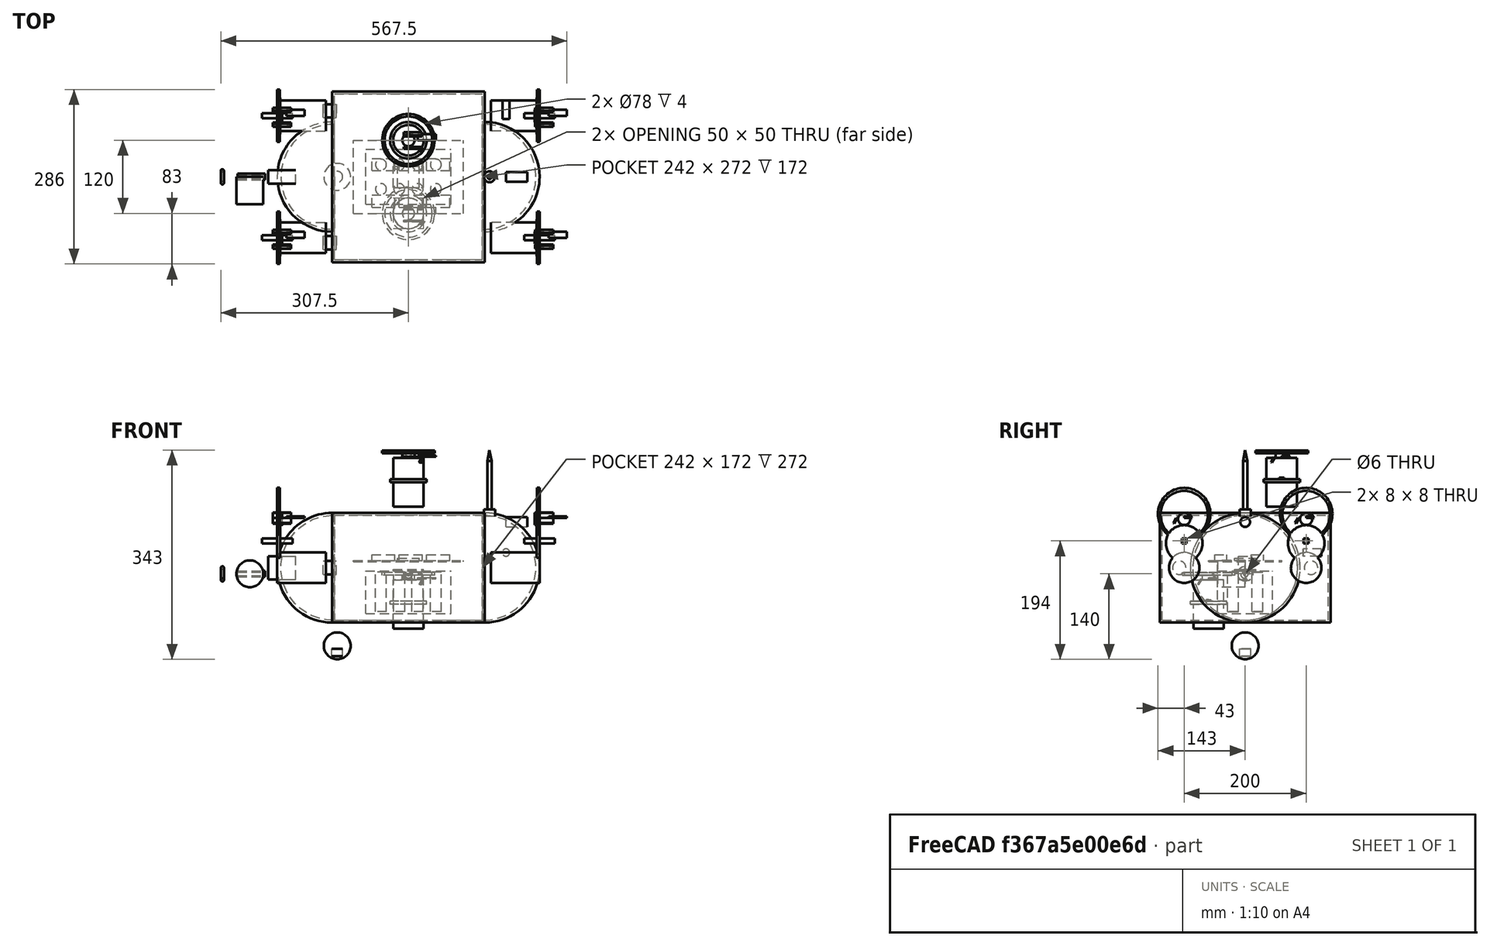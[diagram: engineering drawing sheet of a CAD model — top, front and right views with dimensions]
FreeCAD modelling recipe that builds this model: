
FCSTD DOCUMENT  (FreeCAD 0.19R)
Label: fishing_drone_detailed
License: All rights reserved
LicenseURL: http://en.wikipedia.org/wiki/All_rights_reserved
objects: Part::Cylinder×48, Part::Box×37, Part::MultiFuse×9, Part::Cut×8, Part::Sphere×5, Part::Torus×1, Part::Cone×1
note: 109 computed .brp shape members not serialized (recipe doc carries the construction recipe); baked Part::Feature solids carry a one-line shape summary decoded from their .brp

FEATURE [Part::Box] CenterBody
  AttacherType = Attacher::AttachEngine3D
  Height = 180
  Length = 250
  Placement = pos=(-125,-140,-90) rot=(0,0,1;0rad)
  Width = 280
FEATURE [Part::Sphere] Nose
  Angle1 = -90
  Angle2 = 90
  Angle3 = 360
  AttacherType = Attacher::AttachEngine3D
  Placement = pos=(-125,0,0) rot=(0,0,1;0rad)
  Radius = 90
FEATURE [Part::Sphere] Tail
  Angle1 = -90
  Angle2 = 90
  Angle3 = 360
  AttacherType = Attacher::AttachEngine3D
  Placement = pos=(125,0,0) rot=(0,0,1;0rad)
  Radius = 90
FEATURE [Part::MultiFuse] BodyOuter
  Shapes = -> [CenterBody,Nose,Tail]
FEATURE [Part::Box] CenterInner
  AttacherType = Attacher::AttachEngine3D
  Height = 172
  Length = 242
  Placement = pos=(-121,-136,-86) rot=(0,0,1;0rad)
  Width = 272
FEATURE [Part::Sphere] NoseInner
  Angle1 = -90
  Angle2 = 90
  Angle3 = 360
  AttacherType = Attacher::AttachEngine3D
  Placement = pos=(-123,0,0) rot=(0,0,1;0rad)
  Radius = 86
FEATURE [Part::Sphere] TailInner
  Angle1 = -90
  Angle2 = 90
  Angle3 = 360
  AttacherType = Attacher::AttachEngine3D
  Placement = pos=(123,0,0) rot=(0,0,1;0rad)
  Radius = 86
FEATURE [Part::MultiFuse] BodyInner
  Shapes = -> [CenterInner,NoseInner,TailInner]
FEATURE [Part::Cut] HollowBody
  Base = -> BodyOuter
  Tool = -> BodyInner
FEATURE [Part::Cylinder] Motor_FL
  Angle = 360
  AttacherType = Attacher::AttachEngine3D
  Height = 80
  Placement = pos=(-215,100,0) rot=(0,1,0;1.5708rad)
  Radius = 25
FEATURE [Part::Cylinder] Flange_FL
  Angle = 360
  AttacherType = Attacher::AttachEngine3D
  Height = 5
  Placement = pos=(-215,100,40) rot=(0,1,0;1.5708rad)
  Radius = 30
FEATURE [Part::Box] Blade_FL_0
  AttacherType = Attacher::AttachEngine3D
  Height = 2
  Length = 30
  Placement = pos=(-200,100,82) rot=(0,0,1;0rad)
  Width = 10
FEATURE [Part::Box] Blade_FL_1
  AttacherType = Attacher::AttachEngine3D
  Height = 2
  Length = 30
  Placement = pos=(-222.5,112.99,82) rot=(1,0,0;2.0944rad)
  Width = 10
FEATURE [Part::Box] Blade_FL_2
  AttacherType = Attacher::AttachEngine3D
  Height = 2
  Length = 30
  Placement = pos=(-222.5,87.0096,82) rot=(1,0,0;4.18879rad)
  Width = 10
FEATURE [Part::Cylinder] Hub_FL
  Angle = 360
  AttacherType = Attacher::AttachEngine3D
  Height = 8
  Placement = pos=(-215,100,80) rot=(0,1,0;1.5708rad)
  Radius = 10
FEATURE [Part::Cylinder] GuardOut_FL
  Angle = 360
  AttacherType = Attacher::AttachEngine3D
  Height = 4
  Placement = pos=(-215,100,88) rot=(0,1,0;1.5708rad)
  Radius = 43
FEATURE [Part::Cylinder] GuardIn_FL
  Angle = 360
  AttacherType = Attacher::AttachEngine3D
  Height = 6
  Placement = pos=(-215,100,87) rot=(0,1,0;1.5708rad)
  Radius = 39
FEATURE [Part::Cut] Guard_FL
  Base = -> GuardOut_FL
  Tool = -> GuardIn_FL
FEATURE [Part::Box] Arm_FL
  AttacherType = Attacher::AttachEngine3D
  Height = 8
  Length = 50
  Placement = pos=(-240,96,40) rot=(0,0,1;0rad)
  Width = 8
FEATURE [Part::MultiFuse] Thruster_FL
  Shapes = -> [Motor_FL,Flange_FL,Hub_FL,Guard_FL,Arm_FL,Blade_FL_0,Blade_FL_1,Blade_FL_2]
FEATURE [Part::Cylinder] Motor_FR
  Angle = 360
  AttacherType = Attacher::AttachEngine3D
  Height = 80
  Placement = pos=(-215,-100,0) rot=(0,1,0;1.5708rad)
  Radius = 25
FEATURE [Part::Cylinder] Flange_FR
  Angle = 360
  AttacherType = Attacher::AttachEngine3D
  Height = 5
  Placement = pos=(-215,-100,40) rot=(0,1,0;1.5708rad)
  Radius = 30
FEATURE [Part::Box] Blade_FR_0
  AttacherType = Attacher::AttachEngine3D
  Height = 2
  Length = 30
  Placement = pos=(-200,-100,82) rot=(0,0,1;0rad)
  Width = 10
FEATURE [Part::Box] Blade_FR_1
  AttacherType = Attacher::AttachEngine3D
  Height = 2
  Length = 30
  Placement = pos=(-222.5,-87.0096,82) rot=(1,0,0;2.0944rad)
  Width = 10
FEATURE [Part::Box] Blade_FR_2
  AttacherType = Attacher::AttachEngine3D
  Height = 2
  Length = 30
  Placement = pos=(-222.5,-112.99,82) rot=(1,0,0;4.18879rad)
  Width = 10
FEATURE [Part::Cylinder] Hub_FR
  Angle = 360
  AttacherType = Attacher::AttachEngine3D
  Height = 8
  Placement = pos=(-215,-100,80) rot=(0,1,0;1.5708rad)
  Radius = 10
FEATURE [Part::Cylinder] GuardOut_FR
  Angle = 360
  AttacherType = Attacher::AttachEngine3D
  Height = 4
  Placement = pos=(-215,-100,88) rot=(0,1,0;1.5708rad)
  Radius = 43
FEATURE [Part::Cylinder] GuardIn_FR
  Angle = 360
  AttacherType = Attacher::AttachEngine3D
  Height = 6
  Placement = pos=(-215,-100,87) rot=(0,1,0;1.5708rad)
  Radius = 39
FEATURE [Part::Cut] Guard_FR
  Base = -> GuardOut_FR
  Tool = -> GuardIn_FR
FEATURE [Part::Box] Arm_FR
  AttacherType = Attacher::AttachEngine3D
  Height = 8
  Length = 50
  Placement = pos=(-240,-104,40) rot=(0,0,1;0rad)
  Width = 8
FEATURE [Part::MultiFuse] Thruster_FR
  Shapes = -> [Motor_FR,Flange_FR,Hub_FR,Guard_FR,Arm_FR,Blade_FR_0,Blade_FR_1,Blade_FR_2]
FEATURE [Part::Cylinder] Motor_RL
  Angle = 360
  AttacherType = Attacher::AttachEngine3D
  Height = 80
  Placement = pos=(215,100,0) rot=(0,1,0;-1.5708rad)
  Radius = 25
FEATURE [Part::Cylinder] Flange_RL
  Angle = 360
  AttacherType = Attacher::AttachEngine3D
  Height = 5
  Placement = pos=(215,100,40) rot=(0,1,0;-1.5708rad)
  Radius = 30
FEATURE [Part::Box] Blade_RL_0
  AttacherType = Attacher::AttachEngine3D
  Height = 2
  Length = 30
  Placement = pos=(230,100,82) rot=(0,0,1;0rad)
  Width = 10
FEATURE [Part::Box] Blade_RL_1
  AttacherType = Attacher::AttachEngine3D
  Height = 2
  Length = 30
  Placement = pos=(207.5,112.99,82) rot=(1,0,0;2.0944rad)
  Width = 10
FEATURE [Part::Box] Blade_RL_2
  AttacherType = Attacher::AttachEngine3D
  Height = 2
  Length = 30
  Placement = pos=(207.5,87.0096,82) rot=(1,0,0;4.18879rad)
  Width = 10
FEATURE [Part::Cylinder] Hub_RL
  Angle = 360
  AttacherType = Attacher::AttachEngine3D
  Height = 8
  Placement = pos=(215,100,80) rot=(0,1,0;-1.5708rad)
  Radius = 10
FEATURE [Part::Cylinder] GuardOut_RL
  Angle = 360
  AttacherType = Attacher::AttachEngine3D
  Height = 4
  Placement = pos=(215,100,88) rot=(0,1,0;-1.5708rad)
  Radius = 43
FEATURE [Part::Cylinder] GuardIn_RL
  Angle = 360
  AttacherType = Attacher::AttachEngine3D
  Height = 6
  Placement = pos=(215,100,87) rot=(0,1,0;-1.5708rad)
  Radius = 39
FEATURE [Part::Cut] Guard_RL
  Base = -> GuardOut_RL
  Tool = -> GuardIn_RL
FEATURE [Part::Box] Arm_RL
  AttacherType = Attacher::AttachEngine3D
  Height = 8
  Length = 50
  Placement = pos=(190,96,40) rot=(0,0,1;0rad)
  Width = 8
FEATURE [Part::MultiFuse] Thruster_RL
  Shapes = -> [Motor_RL,Flange_RL,Hub_RL,Guard_RL,Arm_RL,Blade_RL_0,Blade_RL_1,Blade_RL_2]
FEATURE [Part::Cylinder] Motor_RR
  Angle = 360
  AttacherType = Attacher::AttachEngine3D
  Height = 80
  Placement = pos=(215,-100,0) rot=(0,1,0;-1.5708rad)
  Radius = 25
FEATURE [Part::Cylinder] Flange_RR
  Angle = 360
  AttacherType = Attacher::AttachEngine3D
  Height = 5
  Placement = pos=(215,-100,40) rot=(0,1,0;-1.5708rad)
  Radius = 30
FEATURE [Part::Box] Blade_RR_0
  AttacherType = Attacher::AttachEngine3D
  Height = 2
  Length = 30
  Placement = pos=(230,-100,82) rot=(0,0,1;0rad)
  Width = 10
FEATURE [Part::Box] Blade_RR_1
  AttacherType = Attacher::AttachEngine3D
  Height = 2
  Length = 30
  Placement = pos=(207.5,-87.0096,82) rot=(1,0,0;2.0944rad)
  Width = 10
FEATURE [Part::Box] Blade_RR_2
  AttacherType = Attacher::AttachEngine3D
  Height = 2
  Length = 30
  Placement = pos=(207.5,-112.99,82) rot=(1,0,0;4.18879rad)
  Width = 10
FEATURE [Part::Cylinder] Hub_RR
  Angle = 360
  AttacherType = Attacher::AttachEngine3D
  Height = 8
  Placement = pos=(215,-100,80) rot=(0,1,0;-1.5708rad)
  Radius = 10
FEATURE [Part::Cylinder] GuardOut_RR
  Angle = 360
  AttacherType = Attacher::AttachEngine3D
  Height = 4
  Placement = pos=(215,-100,88) rot=(0,1,0;-1.5708rad)
  Radius = 43
FEATURE [Part::Cylinder] GuardIn_RR
  Angle = 360
  AttacherType = Attacher::AttachEngine3D
  Height = 6
  Placement = pos=(215,-100,87) rot=(0,1,0;-1.5708rad)
  Radius = 39
FEATURE [Part::Cut] Guard_RR
  Base = -> GuardOut_RR
  Tool = -> GuardIn_RR
FEATURE [Part::Box] Arm_RR
  AttacherType = Attacher::AttachEngine3D
  Height = 8
  Length = 50
  Placement = pos=(190,-104,40) rot=(0,0,1;0rad)
  Width = 8
FEATURE [Part::MultiFuse] Thruster_RR
  Shapes = -> [Motor_RR,Flange_RR,Hub_RR,Guard_RR,Arm_RR,Blade_RR_0,Blade_RR_1,Blade_RR_2]
FEATURE [Part::Cylinder] Motor_TV
  Angle = 360
  AttacherType = Attacher::AttachEngine3D
  Height = 80
  Placement = pos=(0,60,100) rot=(0,0,1;0rad)
  Radius = 25
FEATURE [Part::Cylinder] Flange_TV
  Angle = 360
  AttacherType = Attacher::AttachEngine3D
  Height = 5
  Placement = pos=(0,60,140) rot=(0,0,1;0rad)
  Radius = 30
FEATURE [Part::Box] Blade_TV_0
  AttacherType = Attacher::AttachEngine3D
  Height = 2
  Length = 30
  Placement = pos=(15,60,182) rot=(0,0,1;0rad)
  Width = 10
FEATURE [Part::Box] Blade_TV_1
  AttacherType = Attacher::AttachEngine3D
  Height = 2
  Length = 30
  Placement = pos=(-7.5,72.9904,182) rot=(1,0,0;2.0944rad)
  Width = 10
FEATURE [Part::Box] Blade_TV_2
  AttacherType = Attacher::AttachEngine3D
  Height = 2
  Length = 30
  Placement = pos=(-7.5,47.0096,182) rot=(1,0,0;4.18879rad)
  Width = 10
FEATURE [Part::Cylinder] Hub_TV
  Angle = 360
  AttacherType = Attacher::AttachEngine3D
  Height = 8
  Placement = pos=(0,60,180) rot=(0,0,1;0rad)
  Radius = 10
FEATURE [Part::Cylinder] GuardOut_TV
  Angle = 360
  AttacherType = Attacher::AttachEngine3D
  Height = 4
  Placement = pos=(0,60,188) rot=(0,0,1;0rad)
  Radius = 43
FEATURE [Part::Cylinder] GuardIn_TV
  Angle = 360
  AttacherType = Attacher::AttachEngine3D
  Height = 6
  Placement = pos=(0,60,187) rot=(0,0,1;0rad)
  Radius = 39
FEATURE [Part::Cut] Guard_TV
  Base = -> GuardOut_TV
  Tool = -> GuardIn_TV
FEATURE [Part::Box] Arm_TV
  AttacherType = Attacher::AttachEngine3D
  Height = 8
  Length = 50
  Placement = pos=(-25,56,140) rot=(0,0,1;0rad)
  Width = 8
FEATURE [Part::MultiFuse] Thruster_TV
  Shapes = -> [Motor_TV,Flange_TV,Hub_TV,Guard_TV,Arm_TV,Blade_TV_0,Blade_TV_1,Blade_TV_2]
FEATURE [Part::Cylinder] Motor_BV
  Angle = 360
  AttacherType = Attacher::AttachEngine3D
  Height = 80
  Placement = pos=(0,-60,-100) rot=(0,0,1;0rad)
  Radius = 25
FEATURE [Part::Cylinder] Flange_BV
  Angle = 360
  AttacherType = Attacher::AttachEngine3D
  Height = 5
  Placement = pos=(0,-60,-60) rot=(0,0,1;0rad)
  Radius = 30
FEATURE [Part::Box] Blade_BV_0
  AttacherType = Attacher::AttachEngine3D
  Height = 2
  Length = 30
  Placement = pos=(15,-60,-18) rot=(0,0,1;0rad)
  Width = 10
FEATURE [Part::Box] Blade_BV_1
  AttacherType = Attacher::AttachEngine3D
  Height = 2
  Length = 30
  Placement = pos=(-7.5,-47.0096,-18) rot=(1,0,0;2.0944rad)
  Width = 10
FEATURE [Part::Box] Blade_BV_2
  AttacherType = Attacher::AttachEngine3D
  Height = 2
  Length = 30
  Placement = pos=(-7.5,-72.9904,-18) rot=(1,0,0;4.18879rad)
  Width = 10
FEATURE [Part::Cylinder] Hub_BV
  Angle = 360
  AttacherType = Attacher::AttachEngine3D
  Height = 8
  Placement = pos=(0,-60,-20) rot=(0,0,1;0rad)
  Radius = 10
FEATURE [Part::Cylinder] GuardOut_BV
  Angle = 360
  AttacherType = Attacher::AttachEngine3D
  Height = 4
  Placement = pos=(0,-60,-12) rot=(0,0,1;0rad)
  Radius = 43
FEATURE [Part::Cylinder] GuardIn_BV
  Angle = 360
  AttacherType = Attacher::AttachEngine3D
  Height = 6
  Placement = pos=(0,-60,-13) rot=(0,0,1;0rad)
  Radius = 39
FEATURE [Part::Cut] Guard_BV
  Base = -> GuardOut_BV
  Tool = -> GuardIn_BV
FEATURE [Part::Box] Arm_BV
  AttacherType = Attacher::AttachEngine3D
  Height = 8
  Length = 50
  Placement = pos=(-25,-64,-60) rot=(0,0,1;0rad)
  Width = 8
FEATURE [Part::MultiFuse] Thruster_BV
  Shapes = -> [Motor_BV,Flange_BV,Hub_BV,Guard_BV,Arm_BV,Blade_BV_0,Blade_BV_1,Blade_BV_2]
FEATURE [Part::Box] BatteryHousing
  AttacherType = Attacher::AttachEngine3D
  Height = 70
  Length = 140
  Placement = pos=(-70,-45,-75) rot=(0,0,1;0rad)
  Width = 90
FEATURE [Part::Cylinder] Cell_0_0
  Angle = 360
  AttacherType = Attacher::AttachEngine3D
  Height = 65
  Placement = pos=(-45,-20,-72) rot=(0,0,1;0rad)
  Radius = 9
FEATURE [Part::Cylinder] Cell_0_1
  Angle = 360
  AttacherType = Attacher::AttachEngine3D
  Height = 65
  Placement = pos=(-45,20,-72) rot=(0,0,1;0rad)
  Radius = 9
FEATURE [Part::Cylinder] Cell_1_0
  Angle = 360
  AttacherType = Attacher::AttachEngine3D
  Height = 65
  Placement = pos=(-15,-20,-72) rot=(0,0,1;0rad)
  Radius = 9
FEATURE [Part::Cylinder] Cell_1_1
  Angle = 360
  AttacherType = Attacher::AttachEngine3D
  Height = 65
  Placement = pos=(-15,20,-72) rot=(0,0,1;0rad)
  Radius = 9
FEATURE [Part::Cylinder] Cell_2_0
  Angle = 360
  AttacherType = Attacher::AttachEngine3D
  Height = 65
  Placement = pos=(15,-20,-72) rot=(0,0,1;0rad)
  Radius = 9
FEATURE [Part::Cylinder] Cell_2_1
  Angle = 360
  AttacherType = Attacher::AttachEngine3D
  Height = 65
  Placement = pos=(15,20,-72) rot=(0,0,1;0rad)
  Radius = 9
FEATURE [Part::Cylinder] Cell_3_0
  Angle = 360
  AttacherType = Attacher::AttachEngine3D
  Height = 65
  Placement = pos=(45,-20,-72) rot=(0,0,1;0rad)
  Radius = 9
FEATURE [Part::Cylinder] Cell_3_1
  Angle = 360
  AttacherType = Attacher::AttachEngine3D
  Height = 65
  Placement = pos=(45,20,-72) rot=(0,0,1;0rad)
  Radius = 9
FEATURE [Part::Box] BMS
  AttacherType = Attacher::AttachEngine3D
  Height = 2
  Length = 50
  Placement = pos=(-25,-17.5,-5) rot=(0,0,1;0rad)
  Width = 35
FEATURE [Part::Box] MainPCB
  AttacherType = Attacher::AttachEngine3D
  Height = 1.6
  Length = 180
  Placement = pos=(-90,-60,10) rot=(0,0,1;0rad)
  Width = 120
FEATURE [Part::Box] MCU
  AttacherType = Attacher::AttachEngine3D
  Height = 4
  Length = 35
  Placement = pos=(-17.5,-17.5,11.6) rot=(0,0,1;0rad)
  Width = 35
FEATURE [Part::Box] ESC_0
  AttacherType = Attacher::AttachEngine3D
  Height = 10
  Length = 38
  Placement = pos=(-60,-50,11.6) rot=(0,0,1;0rad)
  Width = 20
FEATURE [Part::Box] ESC_1
  AttacherType = Attacher::AttachEngine3D
  Height = 10
  Length = 38
  Placement = pos=(-15,-50,11.6) rot=(0,0,1;0rad)
  Width = 20
FEATURE [Part::Box] ESC_2
  AttacherType = Attacher::AttachEngine3D
  Height = 10
  Length = 38
  Placement = pos=(30,-50,11.6) rot=(0,0,1;0rad)
  Width = 20
FEATURE [Part::Box] ESC_3
  AttacherType = Attacher::AttachEngine3D
  Height = 10
  Length = 38
  Placement = pos=(-60,10,11.6) rot=(0,0,1;0rad)
  Width = 20
FEATURE [Part::Box] ESC_4
  AttacherType = Attacher::AttachEngine3D
  Height = 10
  Length = 38
  Placement = pos=(-15,10,11.6) rot=(0,0,1;0rad)
  Width = 20
FEATURE [Part::Box] ESC_5
  AttacherType = Attacher::AttachEngine3D
  Height = 10
  Length = 38
  Placement = pos=(30,10,11.6) rot=(0,0,1;0rad)
  Width = 20
FEATURE [Part::Cylinder] PowerConnector
  Angle = 360
  AttacherType = Attacher::AttachEngine3D
  Height = 35
  Placement = pos=(160,0,75) rot=(0,1,0;1.5708rad)
  Radius = 8
FEATURE [Part::Cylinder] CommConnector
  Angle = 360
  AttacherType = Attacher::AttachEngine3D
  Height = 30
  Placement = pos=(160,125,25) rot=(1,0,0;1.5708rad)
  Radius = 6
FEATURE [Part::Box] ServoBox
  AttacherType = Attacher::AttachEngine3D
  Height = 38
  Length = 45
  Placement = pos=(-230,-11,-19) rot=(0,0,1;0rad)
  Width = 22
FEATURE [Part::Cylinder] LineSpool
  Angle = 360
  AttacherType = Attacher::AttachEngine3D
  Height = 45
  Placement = pos=(-260,0,-10) rot=(1,0,0;1.5708rad)
  Radius = 22
FEATURE [Part::Cylinder] GuideOuter
  Angle = 360
  AttacherType = Attacher::AttachEngine3D
  Height = 45
  Placement = pos=(-280,0,-10) rot=(0,1,0;1.5708rad)
  Radius = 5
FEATURE [Part::Cylinder] GuideInner
  Angle = 360
  AttacherType = Attacher::AttachEngine3D
  Height = 50
  Placement = pos=(-282,0,-10) rot=(0,1,0;1.5708rad)
  Radius = 3
FEATURE [Part::Cut] LineGuide
  Base = -> GuideOuter
  Tool = -> GuideInner
FEATURE [Part::Torus] HookRing
  Angle1 = -180
  Angle2 = 180
  Angle3 = 360
  AttacherType = Attacher::AttachEngine3D
  Placement = pos=(-305,0,-10) rot=(0,1,0;1.5708rad)
  Radius1 = 10
  Radius2 = 2.5
FEATURE [Part::Sphere] CameraHousing
  Angle1 = -90
  Angle2 = 90
  Angle3 = 360
  AttacherType = Attacher::AttachEngine3D
  Placement = pos=(-116.667,0,-128) rot=(0,0,1;0rad)
  Radius = 22
FEATURE [Part::Cylinder] Lens
  Angle = 360
  AttacherType = Attacher::AttachEngine3D
  Height = 12
  Placement = pos=(-116.667,0,-145) rot=(0,0,1;0rad)
  Radius = 9
FEATURE [Part::Cylinder] LED_Left
  Angle = 360
  AttacherType = Attacher::AttachEngine3D
  Height = 22
  Placement = pos=(-140,108,0) rot=(0,1,0;1.5708rad)
  Radius = 11
FEATURE [Part::Cylinder] LED_Right
  Angle = 360
  AttacherType = Attacher::AttachEngine3D
  Height = 22
  Placement = pos=(-140,-108,0) rot=(0,1,0;1.5708rad)
  Radius = 11
FEATURE [Part::Cylinder] AntennaMast
  Angle = 360
  AttacherType = Attacher::AttachEngine3D
  Height = 85
  Placement = pos=(133,0,90) rot=(0,0,1;0rad)
  Radius = 3.5
FEATURE [Part::Cone] AntennaTip
  Angle = 360
  AttacherType = Attacher::AttachEngine3D
  Height = 18
  Placement = pos=(133,0,175) rot=(0,0,1;0rad)
  Radius1 = 3.5
  Radius2 = 0
FEATURE [Part::Cylinder] AntennaBase
  Angle = 360
  AttacherType = Attacher::AttachEngine3D
  Height = 12
  Placement = pos=(133,0,84) rot=(0,0,1;0rad)
  Radius = 9
FEATURE [Part::MultiFuse] Antenna
  Shapes = -> [AntennaMast,AntennaTip,AntennaBase]
